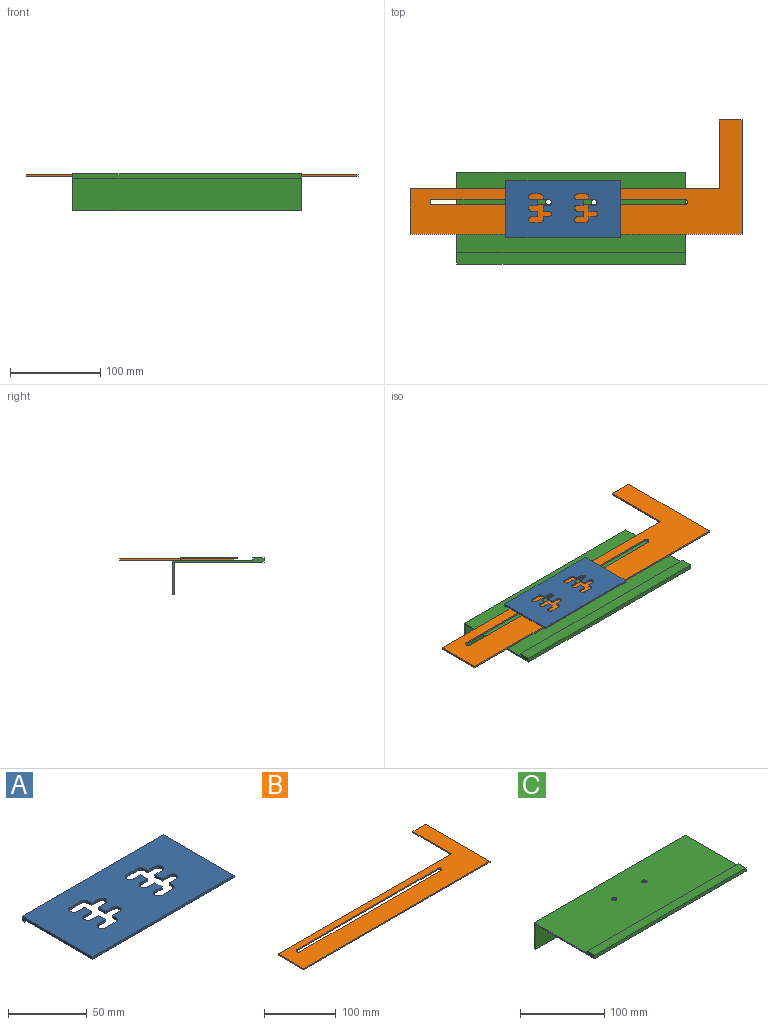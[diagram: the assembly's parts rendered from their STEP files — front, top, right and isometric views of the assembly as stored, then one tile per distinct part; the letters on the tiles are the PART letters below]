
ASSEMBLY  parts=3 mates=2
PART A: 52 faces, bbox 127x63.5x3.6 mm
  f0: plane 127x1.8mm, normal (0,0,-1), area 229mm2, adj f1,f5,f6,f7
  f1: plane 127x3.61mm, normal (0,1,0), area 458.1mm2, adj f0,f2,f6,f7
  f2: plane 127x63.5mm, normal (0,0,1), area 7108.4mm2, adj f1,f3,f6,f7,f8,f9,f10,f11
  f3: plane 127x1.8mm, normal (0,-1,0), area 229mm2, adj f2,f4,f6,f7
  f4: plane 127x61.7mm, normal (0,0,-1), area 6879.3mm2, adj f3,f5,f6,f7,f8,f9,f10,f11
  f5: plane 127x1.8mm, normal (0,-1,0), area 229mm2, adj f0,f4,f6,f7
  f6: plane 63.5x3.61mm, normal (1,0,0), area 117.8mm2, adj f0,f1,f2,f3,f4,f5
  f7: plane 63.5x3.61mm, normal (-1,0,0), area 117.8mm2, adj f0,f1,f2,f3,f4,f5
  f8: cylinder r=3.17mm len=6.35mm, axis (0,0,1), area 18mm2, adj f2,f4,f9,f29
  f9: plane 9.53x1.8mm, normal (0,1,0), area 17.2mm2, adj f2,f4,f8,f10
  f10: cylinder r=3.17mm len=3.18mm, axis (0,0,1), area 9mm2, adj f2,f4,f9,f11
  f11: plane 3.18x1.8mm, normal (-1,0,0), area 5.7mm2, adj f2,f4,f10,f12
  f12: plane 6.35x1.8mm, normal (0,1,0), area 11.5mm2, adj f2,f4,f11,f13
  f13: cylinder r=3.17mm len=6.35mm, axis (0,0,1), area 18mm2, adj f2,f4,f12,f14
  f14: plane 6.35x1.8mm, normal (0,-1,0), area 11.5mm2, adj f2,f4,f13,f15
  f15: plane 6.35x1.8mm, normal (-1,0,0), area 11.5mm2, adj f2,f4,f14,f16
  f16: plane 6.35x1.8mm, normal (0,1,0), area 11.5mm2, adj f2,f4,f15,f17
  f17: cylinder r=3.17mm len=6.35mm, axis (0,0,1), area 18mm2, adj f2,f4,f16,f18
  f18: plane 6.35x1.8mm, normal (0,-1,0), area 11.5mm2, adj f2,f4,f17,f19
  f19: plane 3.18x1.8mm, normal (-1,0,0), area 5.7mm2, adj f2,f4,f18,f20
  f20: cylinder r=3.17mm len=3.18mm, axis (0,0,1), area 9mm2, adj f2,f4,f19,f21
  f21: plane 9.53x1.8mm, normal (0,-1,0), area 17.2mm2, adj f2,f4,f20,f22
  f22: cylinder r=3.17mm len=6.35mm, axis (0,0,1), area 18mm2, adj f2,f4,f21,f23
  f23: plane 6.35x1.8mm, normal (0,1,0), area 11.5mm2, adj f2,f4,f22,f24
  f24: plane 6.35x1.8mm, normal (1,0,0), area 11.5mm2, adj f2,f4,f23,f25
  f25: plane 6.35x1.8mm, normal (0,-1,0), area 11.5mm2, adj f2,f4,f24,f26
  f26: cylinder r=3.17mm len=6.35mm, axis (0,0,1), area 18mm2, adj f2,f4,f25,f27
  f27: plane 6.35x1.8mm, normal (0,1,0), area 11.5mm2, adj f2,f4,f26,f28
  f28: plane 6.35x1.8mm, normal (1,0,0), area 11.5mm2, adj f2,f4,f27,f29
  f29: plane 6.35x1.8mm, normal (0,-1,0), area 11.5mm2, adj f2,f4,f8,f28
  f30: cylinder r=3.17mm len=6.35mm, axis (0,0,1), area 18mm2, adj f2,f4,f31,f51
  f31: plane 9.53x1.8mm, normal (0,1,0), area 17.2mm2, adj f2,f4,f30,f32
  f32: cylinder r=3.17mm len=3.18mm, axis (0,0,1), area 9mm2, adj f2,f4,f31,f33
  f33: plane 3.18x1.8mm, normal (-1,0,0), area 5.7mm2, adj f2,f4,f32,f34
  f34: plane 6.35x1.8mm, normal (0,1,0), area 11.5mm2, adj f2,f4,f33,f35
  f35: cylinder r=3.17mm len=6.35mm, axis (0,0,1), area 18mm2, adj f2,f4,f34,f36
  f36: plane 6.35x1.8mm, normal (0,-1,0), area 11.5mm2, adj f2,f4,f35,f37
  f37: plane 6.35x1.8mm, normal (-1,0,0), area 11.5mm2, adj f2,f4,f36,f38
  f38: plane 6.35x1.8mm, normal (0,1,0), area 11.5mm2, adj f2,f4,f37,f39
  f39: cylinder r=3.17mm len=6.35mm, axis (0,0,1), area 18mm2, adj f2,f4,f38,f40
  f40: plane 6.35x1.8mm, normal (0,-1,0), area 11.5mm2, adj f2,f4,f39,f41
  f41: plane 3.18x1.8mm, normal (-1,0,0), area 5.7mm2, adj f2,f4,f40,f42
  f42: cylinder r=3.17mm len=3.18mm, axis (0,0,1), area 9mm2, adj f2,f4,f41,f43
  f43: plane 9.53x1.8mm, normal (0,-1,0), area 17.2mm2, adj f2,f4,f42,f44
  f44: cylinder r=3.17mm len=6.35mm, axis (0,0,1), area 18mm2, adj f2,f4,f43,f45
  f45: plane 6.35x1.8mm, normal (0,1,0), area 11.5mm2, adj f2,f4,f44,f46
  f46: plane 6.35x1.8mm, normal (1,0,0), area 11.5mm2, adj f2,f4,f45,f47
  f47: plane 6.35x1.8mm, normal (0,-1,0), area 11.5mm2, adj f2,f4,f46,f48
  f48: cylinder r=3.17mm len=6.35mm, axis (0,0,1), area 18mm2, adj f2,f4,f47,f49
  f49: plane 6.35x1.8mm, normal (0,1,0), area 11.5mm2, adj f2,f4,f48,f50
  f50: plane 6.35x1.8mm, normal (1,0,0), area 11.5mm2, adj f2,f4,f49,f51
  f51: plane 6.35x1.8mm, normal (0,-1,0), area 11.5mm2, adj f2,f4,f30,f50
PART B: 12 faces, bbox 368.3x127x1.8 mm
  f0: plane 368.3x127mm, normal (0,0,-1), area 18839.3mm2, adj f2,f3,f4,f5,f6,f7,f8,f9
  f1: plane 368.3x127mm, normal (0,0,1), area 18839.3mm2, adj f2,f3,f4,f5,f6,f7,f8,f9
  f2: plane 342.9x1.8mm, normal (0,1,0), area 618.4mm2, adj f0,f1,f4,f5
  f3: plane 368.3x1.8mm, normal (0,-1,0), area 664.2mm2, adj f0,f1,f4,f6
  f4: plane 50.8x1.8mm, normal (-1,0,0), area 91.6mm2, adj f0,f1,f2,f3
  f5: plane 76.2x1.8mm, normal (-1,0,0), area 137.4mm2, adj f0,f1,f2,f7
  f6: plane 127x1.8mm, normal (1,0,0), area 229mm2, adj f0,f1,f3,f7
  f7: plane 25.4x1.8mm, normal (0,1,0), area 45.8mm2, adj f0,f1,f5,f6
  f8: cylinder r=3.17mm len=6.35mm, axis (0,0,1), area 18mm2, adj f0,f1,f9,f11
  f9: plane 279.4x1.8mm, normal (0,-1,0), area 503.9mm2, adj f0,f1,f8,f10
  f10: cylinder r=3.17mm len=6.35mm, axis (0,0,1), area 18mm2, adj f0,f1,f9,f11
  f11: plane 279.4x1.8mm, normal (0,1,0), area 503.9mm2, adj f0,f1,f8,f10
PART C: 12 faces, bbox 254x101.6x41.3 mm
  f0: plane 254x38.1mm, normal (0,1,0), area 9677.4mm2, adj f1,f7,f8,f9
  f1: plane 254x88.9mm, normal (0,0,1), area 22517.3mm2, adj f0,f2,f8,f9,f10,f11
  f2: plane 254x3.18mm, normal (0,1,0), area 806.5mm2, adj f1,f3,f8,f9
  f3: plane 254x12.7mm, normal (0,0,1), area 3225.8mm2, adj f2,f4,f8,f9
  f4: plane 254x4.98mm, normal (0,-1,0), area 1264.5mm2, adj f3,f5,f8,f9
  f5: plane 254x99.8mm, normal (0,0,-1), area 25285mm2, adj f4,f6,f8,f9,f10,f11
  f6: plane 254x36.3mm, normal (0,-1,0), area 9219.3mm2, adj f5,f7,f8,f9
  f7: plane 254x1.8mm, normal (0,0,-1), area 458.1mm2, adj f0,f6,f8,f9
  f8: plane 101.6x41.28mm, normal (1,0,0), area 289mm2, adj f0,f1,f2,f3,f4,f5,f6,f7
  f9: plane 101.6x41.28mm, normal (-1,0,0), area 289mm2, adj f0,f1,f2,f3,f4,f5,f6,f7
  f10: cylinder r=3.17mm len=6.35mm, axis (0,0,1), area 36mm2, adj f1,f5
  f11: cylinder r=3.17mm len=6.35mm, axis (0,0,1), area 36mm2, adj f1,f5
PLACE A t=(-9.03,3.48,3.61)mm
PLACE B t=(-7.48,1.01,1.8)mm
PLACE C at identity fixed
MATE planar B.f0 <-> C.f1  axis (0,0,-1) through (24.66,6.51,0.9)mm
MATE planar A.f4 <-> B.f1  axis (0,0,-1) through (-8.9,2.29,2.71)mm
